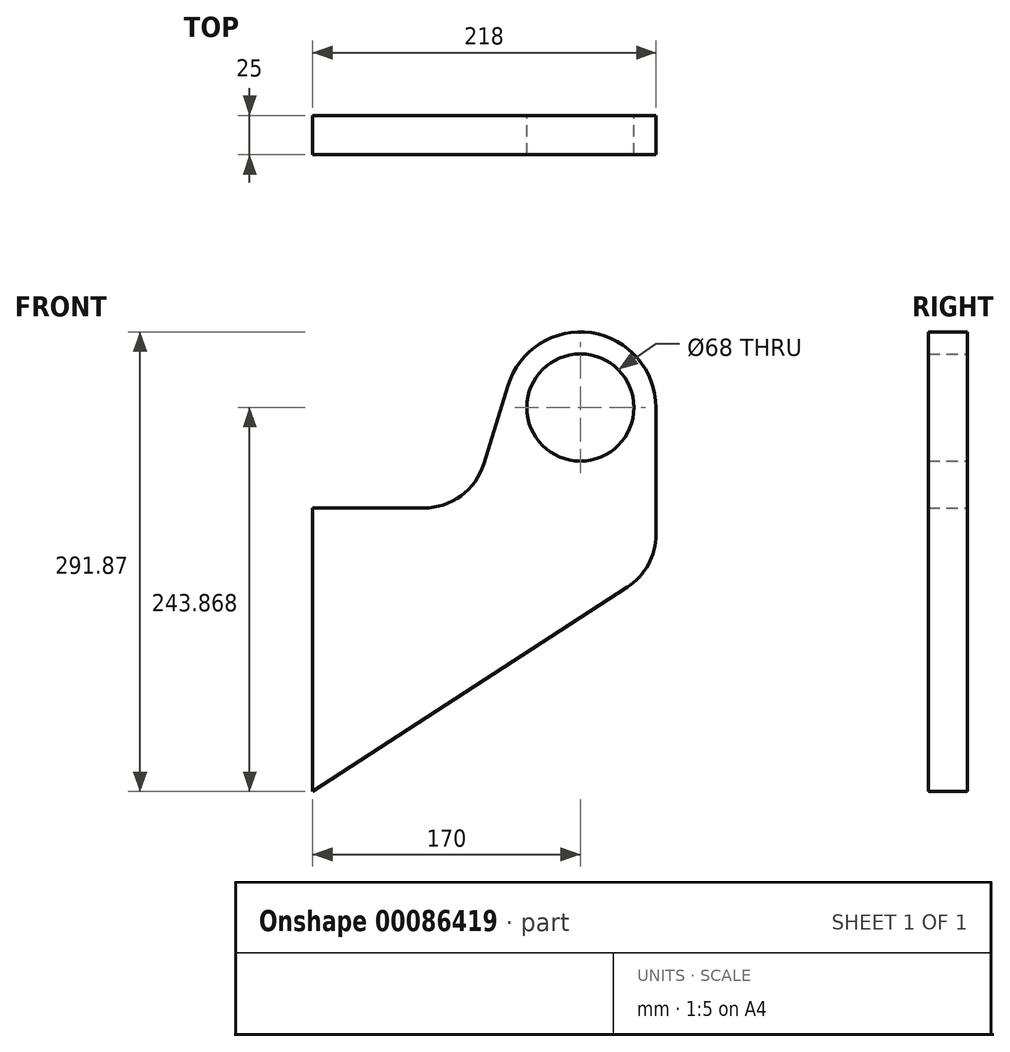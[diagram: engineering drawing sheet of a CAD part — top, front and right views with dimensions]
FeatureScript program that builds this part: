
annotation { "Feature Type Name" : "Feature", "Feature Type Description" : "" }
export const myFeature = defineFeature(function(context is Context, id is Id, definition is map)
    precondition{}
    {
        {
            var Q0;
            Q0=qCreatedBy(makeId("Front.planeOp"),FACE);
            var sketch = newSketch(context, id + "F0", { "sketchPlane" : qUnion([Q0])});
            skLineSegment(sketch, "E0", {"start": v(0, 0) * mm, "end": v(70.5, 0) * mm});
            skLineSegment(sketch, "E1", {"start": v(108.72, 28.18) * mm, "end": v(124.05, 77.73) * mm});
            skLineSegment(sketch, "E2", {"start": v(218, 63.87) * mm, "end": v(218, -16.7) * mm});
            skLineSegment(sketch, "E3", {"start": v(199.79, -50.25) * mm, "end": v(0, -180) * mm});
            skLineSegment(sketch, "E4", {"start": v(0, -180) * mm, "end": v(0, 0) * mm});
            skCircle(sketch, "E5", {"center": v(170, 63.87) * mm, "radius": 48 * mm});
            skCircle(sketch, "E6", {"center": v(170, 63.87) * mm, "radius": 34 * mm});
            skPoint(sketch, "E7.visualSharp", {"position": v(218, -38.43) * mm});
            skArc(sketch, "E7.filletArc", {"start": v(199.79, -50.25) * mm, "mid": v(213.15, -35.8) * mm, "end": v(218, -16.7) * mm});
            skPoint(sketch, "E8.visualSharp", {"position": v(100, 0) * mm});
            skArc(sketch, "E8.filletArc", {"start": v(70.5, 0) * mm, "mid": v(94.24, 7.8) * mm, "end": v(108.72, 28.18) * mm});
            skSolve(sketch);
        }
        {
            var Q0;
            Q0=makeQuery(id+"F0.imprint","IMPRINT",FACE,{"disambiguationData":[TD([[makeQuery(id+"F0.imprint","IMPRINT",EDGE,{"derivedFrom":sQuery(id+"F0.wireOp",EDGE,"E0")}),-1.0]])]});
            var Q1;
            Q1=makeQuery(id+"F0.imprint","IMPRINT",FACE,{"disambiguationData":[TD([[makeQuery(id+"F0.imprint","IMPRINT",EDGE,{"derivedFrom":sQuery(id+"F0.wireOp",EDGE,"E6")}),-1.0]])]});
            extrude(context, id + "F1", {"entities" : qUnion([Q0, Q1]), "depth" : 25 * mm});
        }
        {
            var Q0;
            Q0=makeQuery(id+"F0.imprint","IMPRINT",FACE,{"disambiguationData":[TD([[makeQuery(id+"F0.imprint","IMPRINT",EDGE,{"derivedFrom":sQuery(id+"F0.wireOp",EDGE,"E0")}),-1.0]])]});
            var Q1;
            Q1=makeQuery(id+"F0.imprint","IMPRINT",FACE,{"disambiguationData":[TD([[makeQuery(id+"F0.imprint","IMPRINT",EDGE,{"derivedFrom":sQuery(id+"F0.wireOp",EDGE,"E6")}),-1.0]])]});
            extrude(context, id + "F2", {"entities" : qUnion([Q0, Q1]), "operationType" : NewBodyOperationType.ADD, "depth" : 25 * mm});
        }
    });
